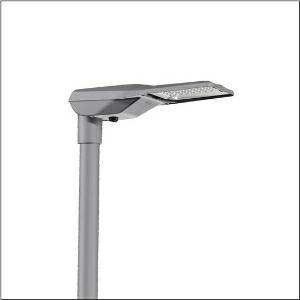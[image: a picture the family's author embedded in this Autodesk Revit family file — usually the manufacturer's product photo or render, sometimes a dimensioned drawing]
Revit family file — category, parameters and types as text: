
# Revit family: streetlight_sl_21_iq_mini___st1_0a_5xe2d31u08jb_b0df
name_source: partatom
category: Lighting Fixtures
units: mm (PartAtom-declared; Revit-internal decimal feet)

## family parameters
Cut with Voids When Loaded = No
Host = Face
Light Source = No
Part Type = Normal
Room Calculation Point = No
Round Connector Dimension = Use Diameter
Shared = No

## types (1)
- --- (1 x LED, 11210 lm, 72.5 W, 3000K)
    Apparent Load = 73 VA
    CIE Flux Codes = 40 73 97 100 100
    Color Rendering = 70
    Color Temperature = 3000K
    Default Elevation = 1800 mm
    Description = Streetlight SL 21 iQ mini, mast luminaire, primary light control with lens, of PMMA, primary optical cover: cover, of toughened safety glass, transparent, light distribution: ST1.0a, light emission: direct distribution, primary light characteristic: asymmetric, installation type: post-top, side-entry, LED, High Power LED, rated luminous flux: 11.210lm, luminous efficacy: 155lm/W, light colour: 730, colour temperature: 3000K, control gear: iQ-Street Remote, D4i with power reduction, control: pre-setting: logarithmic dimming characteristic, Street-Remote, Auto-Match, Temp-Guard, Lumen-Switch, Night-Set, Smart-Wire, Light-Fading, Desk-Remote (wireless, voltage-free reading and setting of iQ features in the workshop via application-optimized NFC function/RFID function), optimised constant luminous flux control (CLO 2.0), mains connection: 220..240V, AC, 50/60Hz, start of lifetime: 73W, end of service life: 76W, reduction: 33W, luminaire housing, of diecast aluminium, powder-coated, Siteco® metallic grey (DB 702S), corrosivity category C5 mid according to DIN EN ISO 12944, please order mast flange separately, inclination adjustable: 0°, 5°, 10°, 15°, sealing non-destructively replaceable, multi-level sealing system, length: 628mm, width: 235mm, height: 110mm, mast flange for spigot size: 42mm (side-entry): 5XC10008XM4, 60/48mm (side-entry/post-top): 5XC10108XM2, 76/60mm (side-entry/post-top): 5XC10108XM1, mounting height: 4..8m, Smart Interface below, protection rating (complete): IP66, insulation class (complete): insulation class II (safety insulation), certification: CE, ENEC, ENEC+, VDE, impact resistance: IK10, permissible operating ambient temperature for outdoor applications: -40..+50°C, standard-compliant lighting for roads and squares, packaging unit: 1 piece

Light Distribution: ST1.0a
    Height = 110 mm
    Lamp = 1 x LED
    Lamp Light Flux = 11210 lm
    Lamp Power = 72.5 W
    Lamp count = 1
    Length = 625 mm
    Luminous efficacy = 155 lm/W
    Manufacturer = Siteco
    ModVariant = No
    Model = 5XE2D31U08JB
    Number of Poles = 1
    OnlyDefault = Yes
    Power Factor = 1
    Product Name = Streetlight SL 21 iQ mini | ST1.0a
    Product group = mast luminaire | pylon top
    ProductGroupID = 6100
    Protection Class = Protection class II
    Protection Degree = IP 66
    RLX_Detail_Level = 1
    RLX_Emergency_Light_Flux = 0 lm
    RLX_Emergency_Type = 0
    RLX_Emergency_Type_DB = No
    RlxData = <blob elided: 92685 chars, md5=8a205e87>
    Socket = socket
    Standby Power = 0 W
    System Light Flux = 11210 lm
    System Power = 73 W
    Type Comments = factory setting: luminous flux: 100 % | dim-lin: 254 | 755 mA
    Type Image = l_1003516.jpg
    URL = http://relux.com
    VarID = @adj_135701
    Voltage = 0 V
    Weight = 0.00 kg
    Width = 234 mm

## geometry (parser evidence)
native form markers: Blend x4, Sweep x12
no freeform markers — native parametric forms only
